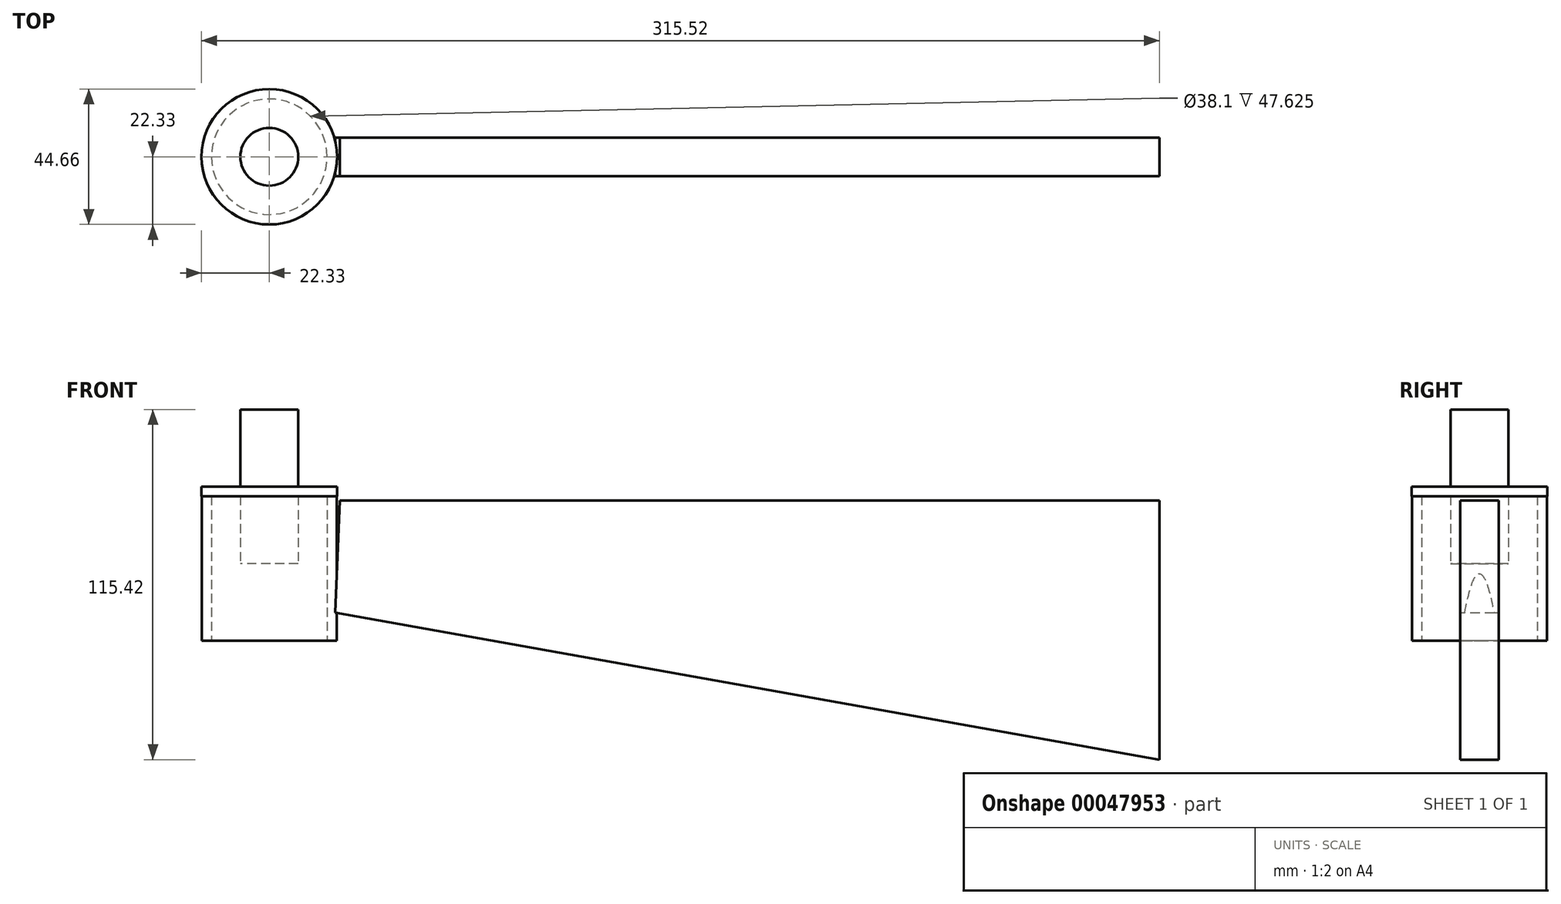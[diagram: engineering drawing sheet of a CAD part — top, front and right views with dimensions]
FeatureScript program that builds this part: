
annotation { "Feature Type Name" : "Feature", "Feature Type Description" : "" }
export const myFeature = defineFeature(function(context is Context, id is Id, definition is map)
    precondition{}
    {
        {
            var Q0;
            Q0=qCreatedBy(makeId("Top.planeOp"),FACE);
            var sketch = newSketch(context, id + "F0", { "sketchPlane" : qUnion([Q0])});
            skCircle(sketch, "E0", {"center": v(0, 0) * mm, "radius": 19.05 * mm});
            skCircle(sketch, "E1", {"center": v(0, 0) * mm, "radius": 22.23 * mm});
            skSolve(sketch);
        }
        {
            var Q0;
            Q0 = qSketchRegion(id + "F0", true);
            extrude(context, id + "F1", {"entities" : qUnion([Q0]), "depth" : 47.62 * mm});
        }
        {
            var Q0;
            Q0=makeQuery(id+"F1.opExtrude","CAP_FACE",FACE,{"disambiguationData":[OSD([sQuery(id+"F0.wireOp",EDGE,"E0"),sQuery(id+"F0.wireOp",EDGE,"E1")])],"isStart":false});
            var sketch = newSketch(context, id + "F2", { "sketchPlane" : qUnion([Q0])});
            skCircle(sketch, "E2", {"center": v(0, 0) * mm, "radius": 22.33 * mm});
            skSolve(sketch);
        }
        {
            var Q0;
            Q0 = qSketchRegion(id + "F2", true);
            extrude(context, id + "F3", {"entities" : qUnion([Q0]), "operationType" : NewBodyOperationType.ADD, "depth" : 3.17 * mm});
        }
        {
            var Q0;
            Q0=makeQuery(id+"F3.opExtrude","CAP_FACE",FACE,{"disambiguationData":[OSD([sQuery(id+"F2.wireOp",EDGE,"E2")])],"isStart":false});
            var sketch = newSketch(context, id + "F4", { "sketchPlane" : qUnion([Q0])});
            skCircle(sketch, "E3", {"center": v(0, 0) * mm, "radius": 9.53 * mm});
            skSolve(sketch);
        }
        {
            var Q0;
            Q0 = qSketchRegion(id + "F4", true);
            extrude(context, id + "F5", {"entities" : qUnion([Q0]), "operationType" : NewBodyOperationType.ADD, "depth" : 25.4 * mm, "hasSecondDirection" : true, "secondDirectionOppositeDirection" : true, "secondDirectionDepth" : 25.4 * mm});
        }
        {
            var Q0;
            Q0=qCreatedBy(makeId("Front.planeOp"),FACE);
            var sketch = newSketch(context, id + "F6", { "sketchPlane" : qUnion([Q0])});
            skLineSegment(sketch, "E4", {"start": v(23.21, 46.23) * mm, "end": v(293.19, 46.23) * mm});
            skLineSegment(sketch, "E5", {"start": v(293.19, 46.23) * mm, "end": v(293.19, -39.23) * mm});
            skLineSegment(sketch, "E6", {"start": v(293.19, -39.23) * mm, "end": v(21.7, 9.17) * mm});
            skLineSegment(sketch, "E7", {"start": v(21.7, 9.17) * mm, "end": v(23.21, 46.23) * mm});
            skSolve(sketch);
        }
        {
            var Q0;
            Q0 = qSketchRegion(id + "F6", true);
            extrude(context, id + "F7", {"entities" : qUnion([Q0]), "operationType" : NewBodyOperationType.ADD, "depth" : 6.35 * mm, "hasSecondDirection" : true, "secondDirectionOppositeDirection" : true, "secondDirectionDepth" : 6.35 * mm});
        }
    });
